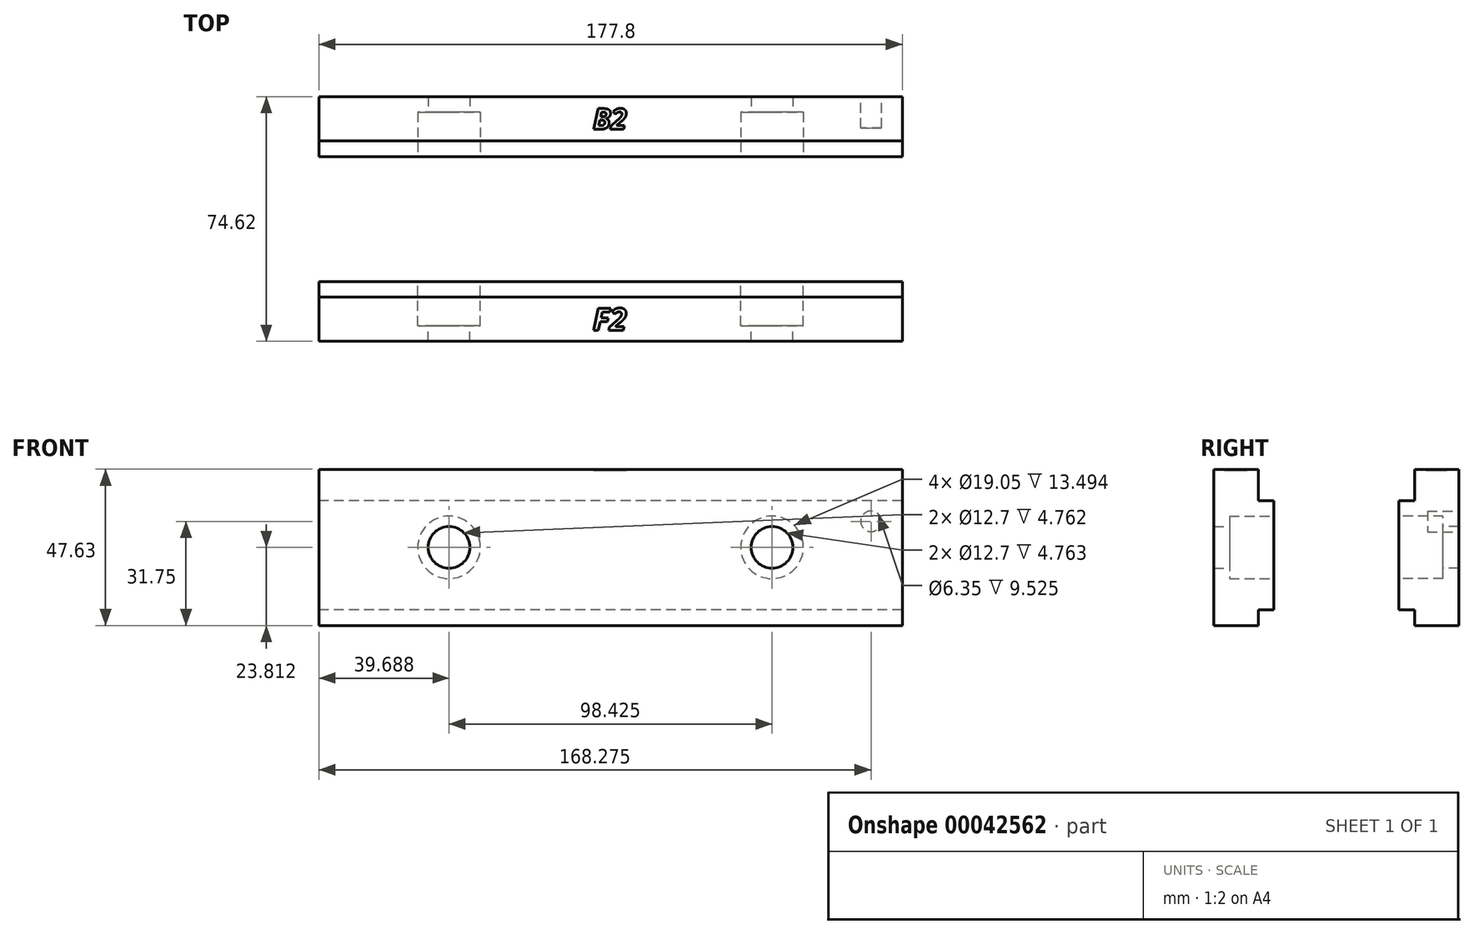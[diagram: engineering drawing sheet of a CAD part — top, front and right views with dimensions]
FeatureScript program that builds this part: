
annotation { "Feature Type Name" : "Feature", "Feature Type Description" : "" }
export const myFeature = defineFeature(function(context is Context, id is Id, definition is map)
    precondition{}
    {
        {
            var Q0;
            Q0=qCreatedBy(makeId("Right.planeOp"),FACE);
            var sketch = newSketch(context, id + "F0", { "sketchPlane" : qUnion([Q0])});
            skLineSegment(sketch, "E0", {"start": v(-17.46, 47.63) * mm, "end": v(-30.96, 47.63) * mm});
            skLineSegment(sketch, "E1", {"start": v(-30.96, 47.63) * mm, "end": v(-30.96, 0) * mm});
            skLineSegment(sketch, "E2", {"start": v(-30.96, 0) * mm, "end": v(-12.7, 0) * mm});
            skLineSegment(sketch, "E3", {"start": v(-12.7, 0) * mm, "end": v(-12.7, 38.1) * mm});
            skLineSegment(sketch, "E4", {"start": v(-12.7, 38.1) * mm, "end": v(-17.46, 38.1) * mm});
            skLineSegment(sketch, "E5", {"start": v(-17.46, 38.1) * mm, "end": v(-17.46, 47.63) * mm});
            skLineSegment(sketch, "E6", {"start": v(0, 0) * mm, "end": v(0, 51.55) * mm, "construction": true});
            skLineSegment(sketch, "E7.MirrorCS", {"start": v(17.46, 47.63) * mm, "end": v(30.96, 47.63) * mm});
            skLineSegment(sketch, "E8.MirrorCS", {"start": v(30.96, 47.63) * mm, "end": v(30.96, 0) * mm});
            skLineSegment(sketch, "E9.MirrorCS", {"start": v(30.96, 0) * mm, "end": v(12.7, 0) * mm});
            skLineSegment(sketch, "E10.MirrorCS", {"start": v(12.7, 38.1) * mm, "end": v(17.46, 38.1) * mm});
            skLineSegment(sketch, "E11.MirrorCS", {"start": v(12.7, 0) * mm, "end": v(12.7, 38.1) * mm});
            skLineSegment(sketch, "E12.MirrorCS", {"start": v(17.46, 38.1) * mm, "end": v(17.46, 47.63) * mm});
            skLineSegment(sketch, "E13", {"start": v(17.46, 0) * mm, "end": v(17.46, 4.76) * mm});
            skLineSegment(sketch, "E14", {"start": v(17.46, 4.76) * mm, "end": v(12.7, 4.76) * mm});
            skLineSegment(sketch, "E15", {"start": v(-12.7, 4.76) * mm, "end": v(-17.46, 4.76) * mm});
            skLineSegment(sketch, "E16", {"start": v(-17.46, 4.76) * mm, "end": v(-17.46, 0) * mm});
            skLineSegment(sketch, "E17", {"start": v(17.46, 4.76) * mm, "end": v(17.46, 38.1) * mm, "construction": true});
            skSolve(sketch);
        }
        {
            var Q0;
            Q0=makeQuery(id+"F0.imprint","IMPRINT",FACE,{"disambiguationData":[TD([[makeQuery(id+"F0.imprint","IMPRINT",EDGE,{"derivedFrom":sQuery(id+"F0.wireOp",EDGE,"E7.MirrorCS")}),-1.0]])]});
            var Q1;
            Q1=makeQuery(id+"F0.imprint","IMPRINT",FACE,{"disambiguationData":[TD([[makeQuery(id+"F0.imprint","IMPRINT",EDGE,{"derivedFrom":sQuery(id+"F0.wireOp",EDGE,"E0")}),1.0]])]});
            extrude(context, id + "F1", {"entities" : qUnion([Q0, Q1]), "depth" : 88.9 * mm, "hasSecondDirection" : true, "secondDirectionOppositeDirection" : true, "secondDirectionDepth" : 88.9 * mm});
        }
        {
            var Q0;
            Q0=makeQuery(id+"F1.opExtrude","SWEPT_FACE",FACE,{"disambiguationData":[OSD([sQuery(id+"F0.wireOp",EDGE,"E3")])]});
            var sketch = newSketch(context, id + "F2", { "sketchPlane" : qUnion([Q0])});
            skPoint(sketch, "E18", {"position": v(-49.21, 23.81) * mm});
            skPoint(sketch, "E19", {"position": v(49.21, 23.81) * mm});
            skLineSegment(sketch, "E20", {"start": v(-49.21, 23.81) * mm, "end": v(49.21, 23.81) * mm, "construction": true});
            skLineSegment(sketch, "E21", {"start": v(0, 23.81) * mm, "end": v(0, 0) * mm, "construction": true});
            skSolve(sketch);
        }
        {
            var Q0;
            Q0=sQuery(id+"F2.wireOp",VERTEX,"E18");
            var Q1;
            Q1=sQuery(id+"F2.wireOp",VERTEX,"E19");
            var Q2;
            Q2=makeQuery(id+"F1.opExtrude","SWEPT_BODY",BODY,{"disambiguationData":[OSD([sQuery(id+"F0.wireOp",EDGE,"E0"),sQuery(id+"F0.wireOp",EDGE,"E1"),sQuery(id+"F0.wireOp",EDGE,"E2"),sQuery(id+"F0.wireOp",EDGE,"E3"),sQuery(id+"F0.wireOp",EDGE,"E4"),sQuery(id+"F0.wireOp",EDGE,"E5")])]});
            hole(context, id + "F3", {"style" : HoleStyle.C_BORE, "endStyle" : HoleEndStyle.THROUGH, "holeDiameter" : 12.7 * mm, "cBoreDiameter" : 19.05 * mm, "cBoreDepth" : 13.5 * mm, "locations" : qUnion([Q0, Q1]), "scope" : qUnion([Q2]), "isTappedThrough" : true});
        }
        {
            var Q0;
            Q0=makeQuery(id+"F1.opExtrude","SWEPT_FACE",FACE,{"disambiguationData":[OSD([sQuery(id+"F0.wireOp",EDGE,"E11.MirrorCS")])]});
            var sketch = newSketch(context, id + "F4", { "sketchPlane" : qUnion([Q0])});
            skPoint(sketch, "E22.0", {"position": v(49.21, 23.81) * mm});
            skPoint(sketch, "E22.1", {"position": v(-49.21, 23.81) * mm});
            skSolve(sketch);
        }
        {
            var Q0;
            Q0=sQuery(id+"F4.wireOp",VERTEX,"E22.1");
            var Q1;
            Q1=sQuery(id+"F4.wireOp",VERTEX,"E22.0");
            var Q2;
            Q2=makeQuery(id+"F1.opExtrude","SWEPT_BODY",BODY,{"disambiguationData":[OSD([sQuery(id+"F0.wireOp",EDGE,"E7.MirrorCS"),sQuery(id+"F0.wireOp",EDGE,"E8.MirrorCS"),sQuery(id+"F0.wireOp",EDGE,"E9.MirrorCS"),sQuery(id+"F0.wireOp",EDGE,"E10.MirrorCS"),sQuery(id+"F0.wireOp",EDGE,"E11.MirrorCS"),sQuery(id+"F0.wireOp",EDGE,"E12.MirrorCS")])]});
            hole(context, id + "F5", {"style" : HoleStyle.C_BORE, "endStyle" : HoleEndStyle.THROUGH, "holeDiameter" : 12.7 * mm, "cBoreDiameter" : 19.05 * mm, "cBoreDepth" : 13.5 * mm, "locations" : qUnion([Q0, Q1]), "scope" : qUnion([Q2]), "isTappedThrough" : true});
        }
        {
            var Q0;
            Q0=makeQuery(id+"F1.opExtrude","SWEPT_FACE",FACE,{"disambiguationData":[OSD([sQuery(id+"F0.wireOp",EDGE,"E8.MirrorCS")])]});
            var sketch = newSketch(context, id + "F6", { "sketchPlane" : qUnion([Q0])});
            skCircle(sketch, "E23", {"center": v(-78.58, 23.81) * mm, "radius": 3.18 * mm, "construction": true});
            skLineSegment(sketch, "E24", {"start": v(-78.58, 23.81) * mm, "end": v(-49.21, 23.81) * mm, "construction": true});
            skLineSegment(sketch, "E25", {"start": v(-75.4, 74.09) * mm, "end": v(-75.4, 0) * mm, "construction": true});
            skLineSegment(sketch, "E26", {"start": v(75.4, 65.84) * mm, "end": v(75.4, 0) * mm, "construction": true});
            skLineSegment(sketch, "E27", {"start": v(75.4, 0) * mm, "end": v(-75.4, 0) * mm, "construction": true});
            skCircle(sketch, "E28", {"center": v(-79.38, 31.75) * mm, "radius": 3.18 * mm});
            skLineSegment(sketch, "E29", {"start": v(-76.2, 31.75) * mm, "end": v(-49.21, 31.75) * mm, "construction": true});
            skSolve(sketch);
        }
        {
            var Q0;
            Q0 = qSketchRegion(id + "F6", true);
            extrude(context, id + "F7", {"entities" : qUnion([Q0]), "operationType" : NewBodyOperationType.REMOVE, "oppositeDirection" : true, "depth" : 9.52 * mm});
        }
        {
            var Q0;
            Q0=makeQuery(id+"F1.opExtrude","SWEPT_FACE",FACE,{"disambiguationData":[OSD([sQuery(id+"F0.wireOp",EDGE,"E7.MirrorCS")])]});
            var sketch = newSketch(context, id + "F8", { "sketchPlane" : qUnion([Q0])});
            skText(sketch, "E30", { "text": "B2\n", "fontName": "OpenSans-BoldItalic.ttf"});
            skLineSegment(sketch, "E31", {"start": v(-88.9, 24.2) * mm, "end": v(-5.38, 24.2) * mm, "construction": true});
            skLineSegment(sketch, "E32", {"start": v(88.9, 24.2) * mm, "end": v(5.38, 24.2) * mm, "construction": true});
            skText(sketch, "E33", { "text": "F2", "fontName": "OpenSans-BoldItalic.ttf"});
            skLineSegment(sketch, "E34", {"start": v(-5.38, -24.2) * mm, "end": v(-88.9, -24.2) * mm, "construction": true});
            const initialGuessF8  = {"E30": [-0.00538, 0.02103, 1, 0, 0.00635], "E33": [-0.00538, -0.02764, 1, 0, 0.00685]};
            skSetInitialGuess(sketch, initialGuessF8);
            skSolve(sketch);
        }
        {
            var Q0;
            Q0 = qSketchRegion(id + "F8", true);
            extrude(context, id + "F9", {"entities" : qUnion([Q0]), "operationType" : NewBodyOperationType.REMOVE, "oppositeDirection" : true, "depth" : 0.25 * mm});
        }
        {
            var Q0;
            Q0=makeQuery(id+"F1.opExtrude","SWEPT_BODY",BODY,{"disambiguationData":[OSD([sQuery(id+"F0.wireOp",EDGE,"E0"),sQuery(id+"F0.wireOp",EDGE,"E1"),sQuery(id+"F0.wireOp",EDGE,"E2"),sQuery(id+"F0.wireOp",EDGE,"E3"),sQuery(id+"F0.wireOp",EDGE,"E4"),sQuery(id+"F0.wireOp",EDGE,"E5"),sQuery(id+"F0.wireOp",EDGE,"E15"),sQuery(id+"F0.wireOp",EDGE,"E16")])]});
            var Q1;
            Q1=makeQuery(id+"F1.opExtrude","CAP_EDGE",EDGE,{"disambiguationData":[OSD([sQuery(id+"F0.wireOp",EDGE,"E0")])],"isStart":true});
            transform(context, id + "F10", {"entities" : qUnion([Q0]), "transformType" : TransformType.TRANSLATION_DISTANCE, "transformDirection" : qUnion([Q1]), "distance" : 12.7 * mm, "makeCopy" : false});
        }
    });
